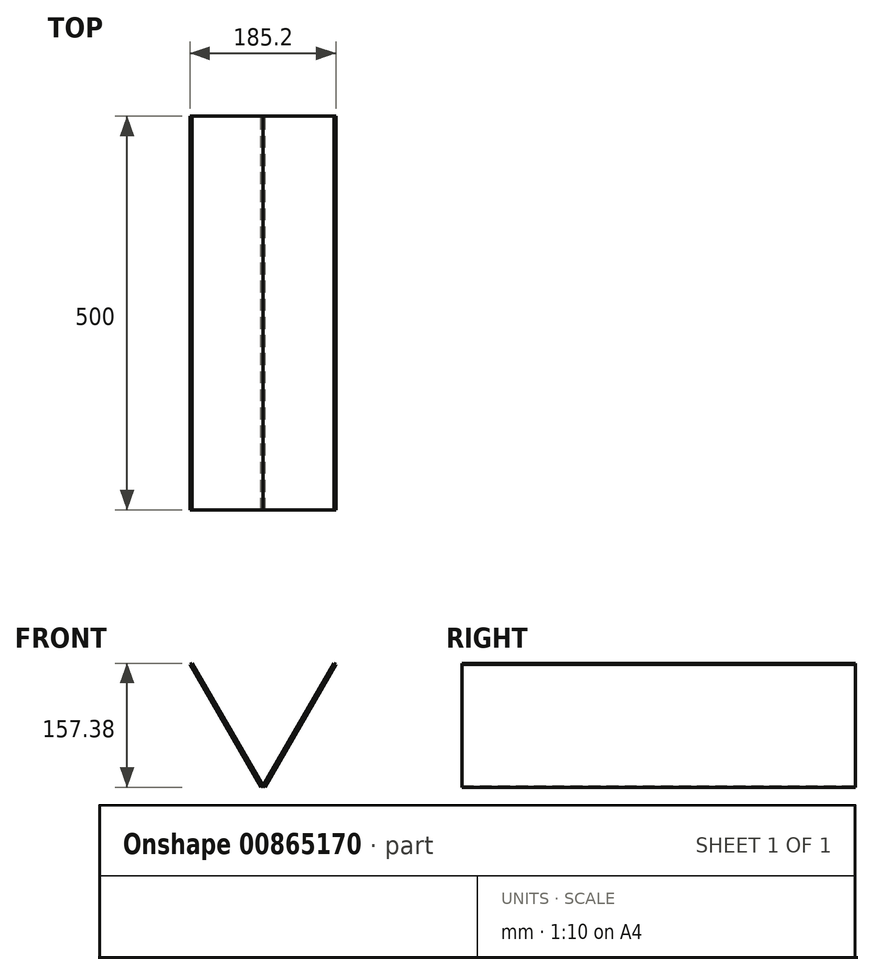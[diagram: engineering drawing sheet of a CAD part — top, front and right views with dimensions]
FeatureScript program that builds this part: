
annotation { "Feature Type Name" : "Feature", "Feature Type Description" : "" }
export const myFeature = defineFeature(function(context is Context, id is Id, definition is map)
    precondition{}
    {
        {
            var Q0;
            Q0=qCreatedBy(makeId("Front.planeOp"),FACE);
            var sketch = newSketch(context, id + "F0", { "sketchPlane" : qUnion([Q0])});
            skLineSegment(sketch, "E0.bottom", {"start": v(-92.6, 154.38) * mm, "end": v(-90, 155.88) * mm});
            skLineSegment(sketch, "E0.top", {"start": v(-2.6, -1.5) * mm, "end": v(0, 0) * mm});
            skLineSegment(sketch, "E0.left", {"start": v(-92.6, 154.38) * mm, "end": v(-2.6, -1.5) * mm});
            skLineSegment(sketch, "E0.right", {"start": v(-90, 155.88) * mm, "end": v(0, 0) * mm});
            skLineSegment(sketch, "E1.MirrorCS", {"start": v(90, 155.88) * mm, "end": v(0, 0) * mm});
            skLineSegment(sketch, "E2.MirrorCS", {"start": v(2.6, -1.5) * mm, "end": v(0, 0) * mm});
            skLineSegment(sketch, "E3.MirrorCS", {"start": v(92.6, 154.38) * mm, "end": v(2.6, -1.5) * mm});
            skLineSegment(sketch, "E4.MirrorCS", {"start": v(92.6, 154.38) * mm, "end": v(90, 155.88) * mm});
            skSolve(sketch);
        }
        {
            var Q0;
            Q0=makeQuery(id+"F0.imprint","IMPRINT",FACE,{"disambiguationData":[TD([[makeQuery(id+"F0.imprint","IMPRINT",EDGE,{"derivedFrom":sQuery(id+"F0.wireOp",EDGE,"E0.bottom")}),-1.0]])]});
            var Q1;
            Q1=makeQuery(id+"F0.imprint","IMPRINT",FACE,{"disambiguationData":[TD([[makeQuery(id+"F0.imprint","IMPRINT",EDGE,{"derivedFrom":sQuery(id+"F0.wireOp",EDGE,"E1.MirrorCS")}),1.0]])]});
            extrude(context, id + "F1", {"entities" : qUnion([Q0, Q1]), "depth" : 500 * mm, "offsetDistance" : 25 * mm});
        }
    });
